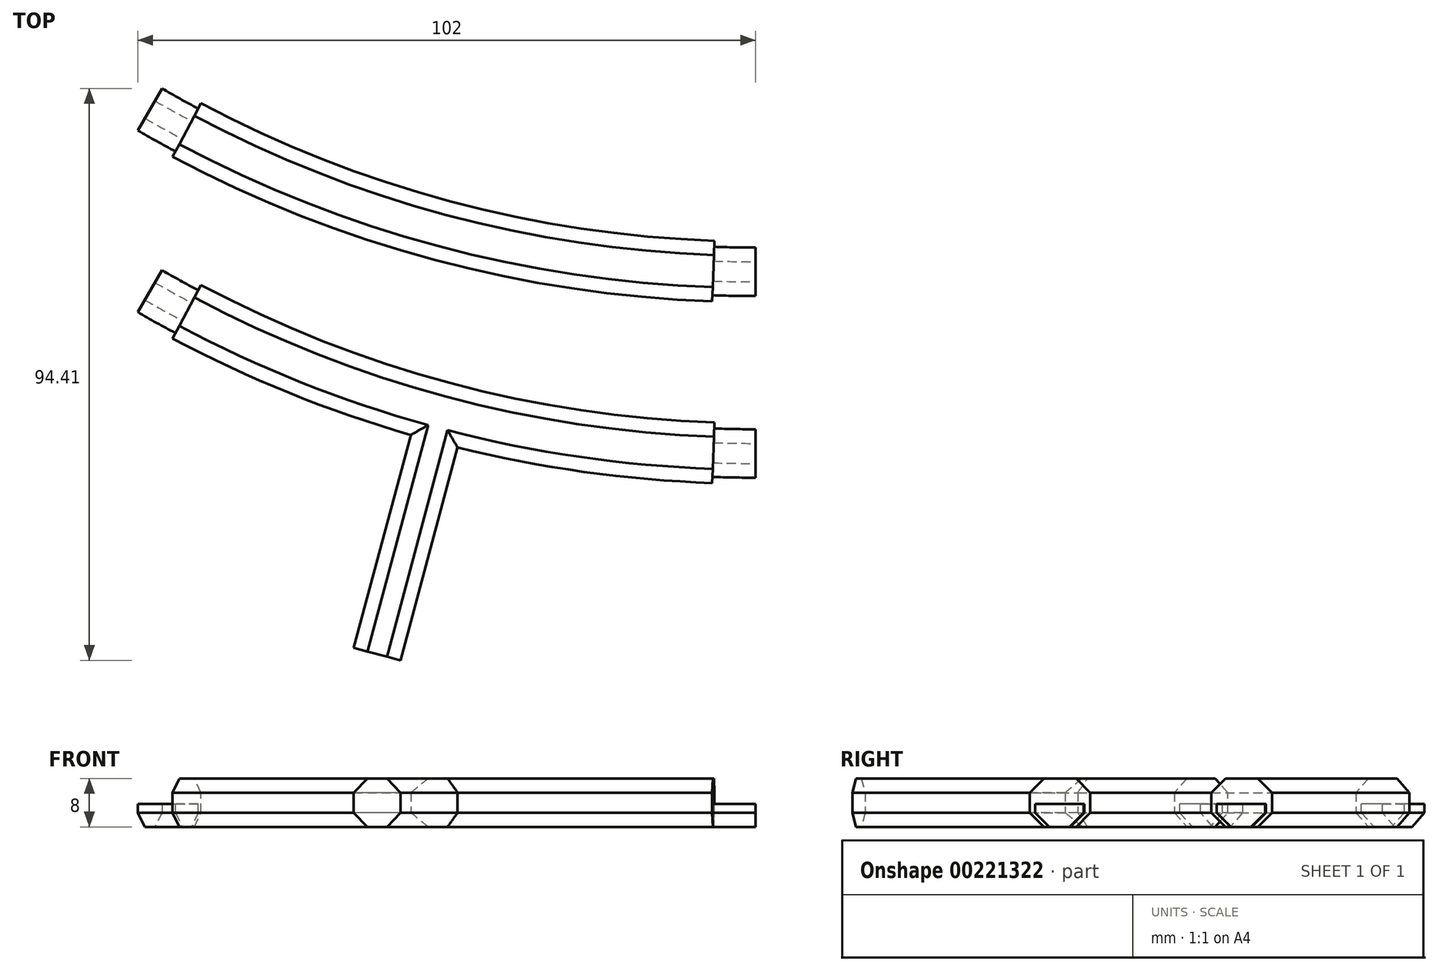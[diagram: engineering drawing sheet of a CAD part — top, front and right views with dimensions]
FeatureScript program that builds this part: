
annotation { "Feature Type Name" : "Feature", "Feature Type Description" : "" }
export const myFeature = defineFeature(function(context is Context, id is Id, definition is map)
    precondition{}
    {
        {
            var Q0;
            Q0=qCreatedBy(makeId("Right.planeOp"),FACE);
            var sketch = newSketch(context, id + "F0", { "sketchPlane" : qUnion([Q0])});
            skCircle(sketch, "E0.cCircle", {"center": v(-200, 0) * mm, "radius": 4 * mm, "construction": true});
            skLineSegment(sketch, "E0.0", {"start": v(-201.66, 4) * mm, "end": v(-198.34, 4) * mm, "construction": true});
            skLineSegment(sketch, "E0.1", {"start": v(-198.34, 4) * mm, "end": v(-196, 1.66) * mm, "construction": true});
            skLineSegment(sketch, "E0.2", {"start": v(-196, 1.66) * mm, "end": v(-196, -1.66) * mm, "construction": true});
            skLineSegment(sketch, "E0.3", {"start": v(-196, -1.66) * mm, "end": v(-198.34, -4) * mm});
            skLineSegment(sketch, "E0.4", {"start": v(-198.34, -4) * mm, "end": v(-201.66, -4) * mm});
            skLineSegment(sketch, "E0.5", {"start": v(-201.66, -4) * mm, "end": v(-204, -1.66) * mm});
            skLineSegment(sketch, "E0.6", {"start": v(-204, -1.66) * mm, "end": v(-204, 1.66) * mm, "construction": true});
            skLineSegment(sketch, "E0.7", {"start": v(-204, 1.66) * mm, "end": v(-201.66, 4) * mm, "construction": true});
            skPoint(sketch, "E0.0.midPoint", {"position": v(-200, 4) * mm});
            skLineSegment(sketch, "E1", {"start": v(-204, -1.66) * mm, "end": v(-204, -0.2) * mm});
            skLineSegment(sketch, "E2", {"start": v(-204, -0.2) * mm, "end": v(-196, -0.2) * mm});
            skLineSegment(sketch, "E3", {"start": v(-196, -0.2) * mm, "end": v(-196, -1.66) * mm});
            skSolve(sketch);
        }
        {
            var Q0;
            Q0=qCreatedBy(makeId("Right.planeOp"),FACE);
            var sketch = newSketch(context, id + "F1", { "sketchPlane" : qUnion([Q0])});
            skLineSegment(sketch, "E4", {"start": v(0, 74.77) * mm, "end": v(0, -44.9) * mm, "construction": true});
            skSolve(sketch);
        }
        {
            var Q0;
            Q0=qCreatedBy(makeId("Right.planeOp"),FACE);
            var sketch = newSketch(context, id + "F2", { "sketchPlane" : qUnion([Q0])});
            skLineSegment(sketch, "E5", {"start": v(-197.34, 4) * mm, "end": v(-202.66, 4) * mm});
            skLineSegment(sketch, "E6", {"start": v(-202.66, 4) * mm, "end": v(-205, 1.66) * mm});
            skLineSegment(sketch, "E7", {"start": v(-205, 1.66) * mm, "end": v(-205, -1.66) * mm});
            skLineSegment(sketch, "E8", {"start": v(-205, -1.66) * mm, "end": v(-202.66, -4) * mm});
            skLineSegment(sketch, "E9", {"start": v(-202.66, -4) * mm, "end": v(-197.34, -4) * mm});
            skLineSegment(sketch, "E10", {"start": v(-197.34, -4) * mm, "end": v(-195, -1.66) * mm});
            skLineSegment(sketch, "E11", {"start": v(-195, -1.66) * mm, "end": v(-195, 1.66) * mm});
            skLineSegment(sketch, "E12", {"start": v(-195, 1.66) * mm, "end": v(-197.34, 4) * mm});
            skLineSegment(sketch, "E13", {"start": v(-200, 4) * mm, "end": v(-200, -4) * mm, "construction": true});
            skLineSegment(sketch, "E14", {"start": v(0, 0) * mm, "end": v(0, 54.23) * mm, "construction": true});
            skSolve(sketch);
        }
        {
            var Q0;
            Q0 = qSketchRegion(id + "F0", true);
            var Q1;
            Q1=sQuery(id+"F1.wireOp",EDGE,"E4");
            revolve(context, id + "F3", {"entities" : qUnion([Q0]), "axis" : qUnion([Q1]), "revolveType" : RevolveType.SYMMETRIC, "angle" : 30 * degree});
        }
        {
            var Q0;
            Q0 = qSketchRegion(id + "F2", true);
            var Q1;
            Q1=sQuery(id+"F2.wireOp",EDGE,"E14");
            revolve(context, id + "F4", {"operationType" : NewBodyOperationType.ADD, "entities" : qUnion([Q0]), "axis" : qUnion([Q1]), "revolveType" : RevolveType.SYMMETRIC, "angle" : 26 * degree});
        }
        {
            var Q0;
            Q0=makeQuery(id+"F3.opRevolve","SWEPT_BODY",BODY,{"disambiguationData":[OSD([sQuery(id+"F0.wireOp",EDGE,"E0.3"),sQuery(id+"F0.wireOp",EDGE,"E0.4"),sQuery(id+"F0.wireOp",EDGE,"E0.5"),sQuery(id+"F0.wireOp",EDGE,"E1"),sQuery(id+"F0.wireOp",EDGE,"E2"),sQuery(id+"F0.wireOp",EDGE,"E3")])]});
            var Q1;
            Q1=sQuery(id+"F1.wireOp",EDGE,"E4");
            transform(context, id + "F5", {"entities" : qUnion([Q0]), "transformType" : TransformType.ROTATION, "transformAxis" : qUnion([Q1]), "angle" : 15 * degree, "makeCopy" : false});
        }
        {
            var Q0;
            Q0=makeQuery(id+"F3.opRevolve","SWEPT_BODY",BODY,{"disambiguationData":[OSD([sQuery(id+"F0.wireOp",EDGE,"E0.3"),sQuery(id+"F0.wireOp",EDGE,"E0.4"),sQuery(id+"F0.wireOp",EDGE,"E0.5"),sQuery(id+"F0.wireOp",EDGE,"E1"),sQuery(id+"F0.wireOp",EDGE,"E2"),sQuery(id+"F0.wireOp",EDGE,"E3")])]});
            transform(context, id + "F6", {"entities" : qUnion([Q0]), "transformType" : TransformType.TRANSLATION_3D, "dx" : 0 * mm, "dy" : -30 * mm, "dz" : 0 * mm, "makeCopy" : true});
        }
        {
            var Q0;
            Q0=makeQuery(id+"F6.opPattern","COPY",EDGE,{"derivedFrom":makeQuery(id+"F4.opRevolve","SWEPT_EDGE",EDGE,{"disambiguationData":[OSD([sQuery(id+"F2.wireOp",EDGE,"E5"),sQuery(id+"F2.wireOp",EDGE,"E12")])]}),"instanceName":"1"});
            cPoint(context, id + "F7", {"entities" : qUnion([Q0]), "parameter" : 0.5});
        }
        {
            var Q0;
            Q0=makeQuery(id+"F6.opPattern","COPY",EDGE,{"derivedFrom":makeQuery(id+"F4.opRevolve","SWEPT_EDGE",EDGE,{"disambiguationData":[OSD([sQuery(id+"F2.wireOp",EDGE,"E5"),sQuery(id+"F2.wireOp",EDGE,"E6")])]}),"instanceName":"1"});
            cPoint(context, id + "F8", {"entities" : qUnion([Q0]), "parameter" : 0.5});
        }
        {
            var Q0;
            Q0=makeQuery(id+"F6.opPattern","COPY",EDGE,{"derivedFrom":makeQuery(id+"F4.opRevolve","SWEPT_EDGE",EDGE,{"disambiguationData":[OSD([sQuery(id+"F2.wireOp",EDGE,"E6"),sQuery(id+"F2.wireOp",EDGE,"E7")])]}),"instanceName":"1"});
            cPoint(context, id + "F9", {"entities" : qUnion([Q0]), "parameter" : 0.5});
        }
        {
            var Q0;
            Q0 = qCreatedBy(id + "F7" ,VERTEX);
            var Q1;
            Q1 = qCreatedBy(id + "F8" ,VERTEX);
            var Q2;
            Q2 = qCreatedBy(id + "F9" ,VERTEX);
            cPlane(context, id + "F10", {"entities" : qUnion([Q0, Q1, Q2]), "cplaneType" : CPlaneType.THREE_POINT, "offset" : 25 * mm, "width" : 150 * mm, "height" : 150 * mm});
        }
        {
            var Q0;
            Q0=qCreatedBy(id+"F10.planeOp",FACE);
            var sketch = newSketch(context, id + "F11", { "sketchPlane" : qUnion([Q0])});
            skLineSegment(sketch, "E15.bottom", {"start": v(270.32, 4) * mm, "end": v(226.32, 4) * mm});
            skLineSegment(sketch, "E15.top", {"start": v(270.32, -4) * mm, "end": v(226.32, -4) * mm});
            skLineSegment(sketch, "E15.left", {"start": v(270.32, 4) * mm, "end": v(270.32, -4) * mm});
            skLineSegment(sketch, "E15.right", {"start": v(226.32, 4) * mm, "end": v(226.32, -4) * mm});
            skSolve(sketch);
        }
        {
            var Q0;
            Q0 = qSketchRegion(id + "F11", true);
            extrude(context, id + "F12", {"entities" : qUnion([Q0]), "operationType" : NewBodyOperationType.ADD, "endBound" : BoundingType.SYMMETRIC, "depth" : 8 * mm});
        }
        {
            var Q0;
            Q0=makeQuery(id+"F12.opExtrude","CAP_EDGE",EDGE,{"disambiguationData":[OSD([sQuery(id+"F11.wireOp",EDGE,"E15.bottom")])],"isStart":true});
            var Q1;
            Q1=makeQuery(id+"F12.opExtrude","CAP_EDGE",EDGE,{"disambiguationData":[OSD([sQuery(id+"F11.wireOp",EDGE,"E15.bottom")])],"isStart":false});
            var Q2;
            Q2=makeQuery(id+"F12.opExtrude","CAP_EDGE",EDGE,{"disambiguationData":[OSD([sQuery(id+"F11.wireOp",EDGE,"E15.top")])],"isStart":true});
            var Q3;
            Q3=makeQuery(id+"F12.opExtrude","CAP_EDGE",EDGE,{"disambiguationData":[OSD([sQuery(id+"F11.wireOp",EDGE,"E15.top")])],"isStart":false});
            chamfer(context, id + "F13", {"entities" : qUnion([Q0, Q1, Q2, Q3]), "width" : ((8 - 3.31) / 2) * mm, "tangentPropagation" : true});
        }
    });
